# Revit family: PRD_FrankeWS_JntrlUnits_SiriusCleanersSink_F832V,F832V-F
name_source: partatom
category: Plumbing Fixtures
revit_build: Autodesk Revit 2018 (Build: 20190510_1515(x64)
units: mm (PartAtom-declared; Revit-internal decimal feet)

## family parameters
Always vertical = Yes
Cut with Voids When Loaded = No
OmniClass Number = 23.45.05.14.14
OmniClass Title = Sinks/Lavatories
Part Type = Normal
Room Calculation Point = No
Round Connector Dimension = Use Diameter
Shared = No
Work Plane-Based = No

## types (2) — shared parameters
AssetType = Fixed
Category = Pr_40_20_96_44, Janitorial sinks
Color = Stainless steel
DrainSize = DN 40 (1 1/2 inch.)
DurationUnit = year
Finish = Satin finished
FinishAndMaterial = Stainless steel 1.4301
Form = Stainless steel cleaners sink
IfcExportAs = IfcSanitaryTerminalType
IfcExportType = SINK
Manufacturer = KWC Group AG
ManufacturerName = KWC Group AG
ManufacturerURL = www.kwc.com
Material = Stainless steel
NBSDescription = Janitorial units
NBSReference = 45-35-70/401
NominalDepth = 598 mm  [stored 1.96194 ft]
NominalHeight = 700 mm  [stored 2.29659 ft]
NominalWidth = 600 mm
ProductInformation = https://pim.kwc.com
Shape = Rectangular
SinkMaterial = PRD_AR_StainlessSteel_SatinFinished
SinkMounting = Pedestal
SinkType = Other
Size = 600 x 598 x 700 mm
URL = www.kwc.com
Uniclass2015Code = Pr_40_20_96_44
Uniclass2015Title = Janitorial sinks
Uniclass2015Version = Products v1.5
Version = 1
WarrantyDurationUnit = year
WasteSize = 40  [stored 0.131234 ft]
WaterSupplyOverflowAndWasteHolesOverflow = Stand pipe overflow
WaterSupplyOverflowAndWasteHolesWaste = Left-Back-Corner
WaterSupplyOverflowAndWasteHolesWaterSupply = No tapholes

## per-type parameters (varying)
| type | BIMObjectName | Description | Features | GrossWeight | ModelNumber | Name | NetWeight |
| F832V-F | PRD_AR_JanitorialUnits_SiriusCleanersSink_F832V-F | Floor standing cleaners sink, stainless steel, surface satin finished, material thickness 1 mm, seamless welded bowl with diameter 450x450x250 mm, bowl with revolving channel, without tap ledge and 50 mm rear upstand, 1 1/2'' plug waste with stainless steel overflow tube, drainage back left, incl. stainless steel folding grid with rubber bumps, underframe with 300 mm aprons, cross stud on backside for better stability, 650 mm working height, feet 40x40 mm and height adjustable to 25 mm. Floor standing janitorial unit with base welded together. | stainless steel, 1.00 mm, satin finished, floor mounting, 600x700x598 mm (WxHxD) | 19.40 kg | 2000057046 | Sirius cleaners sink F832V-F | 19.00 kg |
| F832V | PRD_AR_JanitorialUnits_SiriusCleanersSink_F832V | Floor standing cleaners sink, stainless steel, surface satin finished, material thickness 1 mm, seamless welded bowl with diameter 450x450x250 mm, bowl with revolving channel, without tap ledge and 50 mm rear upstand, 1 1/2'' plug waste with stainless steel overflow tube, drainage back left, incl. stainless steel folding grid with rubber bumps, underframe with 300 mm aprons, cross stud on backside for better stability, 650 mm working height, feet 40x40 mm and height adjustable to 25 mm. Floor standing janitorial unit for screwing. | stainless steel, 1.00 mm, satin finished, no mounting, 600x700x598 mm (WxHxD) | 47.50 kg | 2000100061 | Sirius cleaners sink F832V | 24.50 kg |

note: column(s) folded — value = type name in every type: Model, ModelReference

note: [stored X ft] marks values corroborated as IEEE doubles in the binary element streams (Revit-internal decimal feet)

## geometry (parser evidence)
native form markers: Sweep x6
no freeform markers — native parametric forms only
